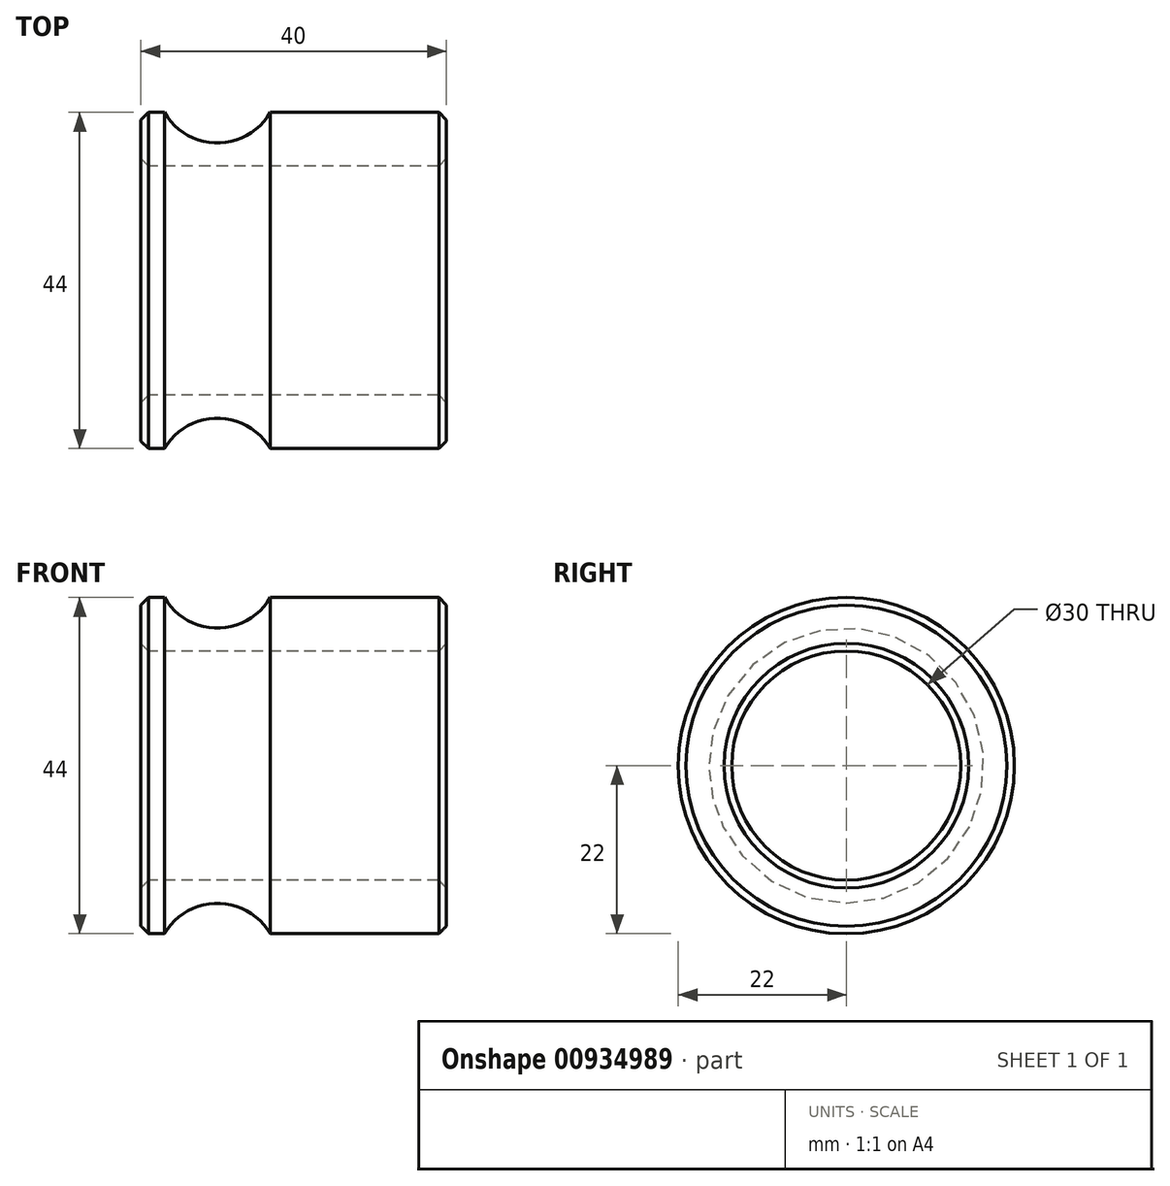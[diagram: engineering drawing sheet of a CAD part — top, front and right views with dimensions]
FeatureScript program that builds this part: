
annotation { "Feature Type Name" : "Feature", "Feature Type Description" : "" }
export const myFeature = defineFeature(function(context is Context, id is Id, definition is map)
    precondition{}
    {
        {
            var Q0;
            Q0=qCreatedBy(makeId("Front.planeOp"),FACE);
            var sketch = newSketch(context, id + "F0", { "sketchPlane" : qUnion([Q0])});
            skCircle(sketch, "E0", {"center": v(-10, 26) * mm, "radius": 8 * mm});
            skCircle(sketch, "E1.MirrorC", {"center": v(10, 26) * mm, "radius": 8 * mm});
            skLineSegment(sketch, "E2", {"start": v(-10, 0) * mm, "end": v(10, 0) * mm, "construction": true});
            skSolve(sketch);
        }
        {
            var Q0;
            Q0=qCreatedBy(makeId("Front.planeOp"),FACE);
            var sketch = newSketch(context, id + "F1", { "sketchPlane" : qUnion([Q0])});
            skLineSegment(sketch, "E3.bottom", {"start": v(20, 22) * mm, "end": v(-20, 22) * mm});
            skLineSegment(sketch, "E3.top", {"start": v(20, 15) * mm, "end": v(-20, 15) * mm});
            skLineSegment(sketch, "E3.left", {"start": v(20, 22) * mm, "end": v(20, 15) * mm});
            skLineSegment(sketch, "E3.right", {"start": v(-20, 22) * mm, "end": v(-20, 15) * mm});
            skPoint(sketch, "E3.middle", {"position": v(0, 18.5) * mm});
            skSolve(sketch);
        }
        {
            var Q0;
            Q0=makeQuery(id+"F1.imprint","IMPRINT",FACE,{"disambiguationData":[TD([[makeQuery(id+"F1.imprint","IMPRINT",EDGE,{"derivedFrom":sQuery(id+"F1.wireOp",EDGE,"E3.bottom")}),1.0]])]});
            var Q1;
            Q1=sQuery(id+"F0.wireOp",EDGE,"E2");
            var Q2;
            Q2=sQuery(id+"F0.wireOp",EDGE,"E2");
            revolve(context, id + "F2", {"surfaceOperationType" : NewSurfaceOperationType.NEW, "entities" : qUnion([Q0]), "surfaceEntities" : qUnion([Q1]), "axis" : qUnion([Q2]), "revolveType" : RevolveType.FULL});
        }
        {
            var Q0;
            Q0=makeQuery(id+"F2.opRevolve","SWEPT_EDGE",EDGE,{"disambiguationData":[OSD([sQuery(id+"F1.wireOp",EDGE,"E3.bottom"),sQuery(id+"F1.wireOp",EDGE,"E3.right")])]});
            var Q1;
            Q1=makeQuery(id+"F2.opRevolve","SWEPT_EDGE",EDGE,{"disambiguationData":[OSD([sQuery(id+"F1.wireOp",EDGE,"E3.top"),sQuery(id+"F1.wireOp",EDGE,"E3.right")])]});
            var Q2;
            Q2=makeQuery(id+"F2.opRevolve","SWEPT_EDGE",EDGE,{"disambiguationData":[OSD([sQuery(id+"F1.wireOp",EDGE,"E3.bottom"),sQuery(id+"F1.wireOp",EDGE,"E3.left")])]});
            var Q3;
            Q3=makeQuery(id+"F2.opRevolve","SWEPT_EDGE",EDGE,{"disambiguationData":[OSD([sQuery(id+"F1.wireOp",EDGE,"E3.top"),sQuery(id+"F1.wireOp",EDGE,"E3.left")])]});
            chamfer(context, id + "F3", {"entities" : qUnion([Q0, Q1, Q2, Q3]), "width" : 1 * mm, "tangentPropagation" : true});
        }
        {
            var Q0;
            Q0=makeQuery(id+"F0.imprint","IMPRINT",FACE,{"disambiguationData":[TD([[makeQuery(id+"F0.imprint","IMPRINT",EDGE,{"derivedFrom":sQuery(id+"F0.wireOp",EDGE,"E0")}),1.0]])]});
            var Q1;
            Q1=makeQuery(id+"F0.imprint","IMPRINT",FACE,{"disambiguationData":[TD([[makeQuery(id+"F0.imprint","IMPRINT",EDGE,{"derivedFrom":sQuery(id+"F0.wireOp",EDGE,"E1.MirrorC")}),-1.0]])]});
            var Q2;
            Q2=sQuery(id+"F0.wireOp",EDGE,"E2");
            revolve(context, id + "F4", {"operationType" : NewBodyOperationType.REMOVE, "surfaceOperationType" : NewSurfaceOperationType.NEW, "entities" : qUnion([Q0, Q1]), "axis" : qUnion([Q2]), "revolveType" : RevolveType.FULL, "oppositeDirection" : true});
        }
    });
